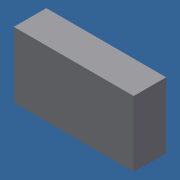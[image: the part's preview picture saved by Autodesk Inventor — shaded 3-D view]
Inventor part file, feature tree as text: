
AUTODESK INVENTOR PART (.ipt)
format: ipt  version: 2014 (Build 180170000, 170)  size: 235,520 bytes
history: native  units: in
note: dims shown in document units (in); Inventor stores cm internally (conversion verified against a paired STEP export)
features: extrude x1, imported_body x1, boolean_combine x1, sketch x1, reference x1
ambient origin geometry x8: Origin, YZ Plane, XZ Plane, XY Plane, X Axis, Y Axis, Z Axis, Center Point
bodies: Solid1 (feature_tree), Solid2 (feature_tree)
feature tree (5):
  extrude  "Extrusion1"  Depth=0.0787in
  imported_body  "Base1"
  boolean_combine  "Combine1"
  sketch  "Sketch1"  dims[d0=0.0787in d1=0.0787in d2=0.0787in d3=0.0787in d4=0.4724in d5=0.0in]
  reference  "Reference1"
